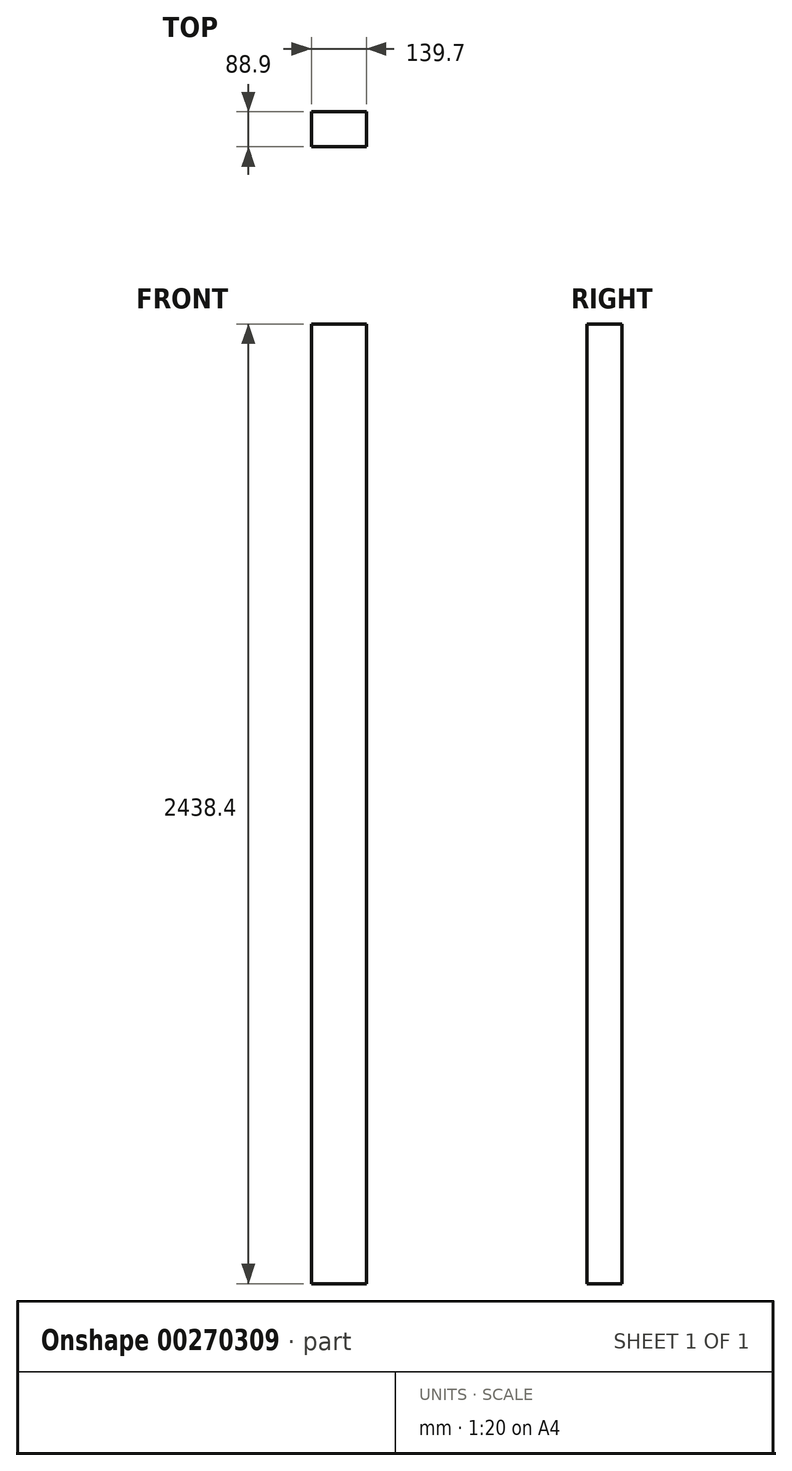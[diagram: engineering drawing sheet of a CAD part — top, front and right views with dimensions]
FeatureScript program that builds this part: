
annotation { "Feature Type Name" : "Feature", "Feature Type Description" : "" }
export const myFeature = defineFeature(function(context is Context, id is Id, definition is map)
    precondition{}
    {
        {
            var Q0;
            Q0=qCreatedBy(makeId("Top.planeOp"),FACE);
            var sketch = newSketch(context, id + "F0", { "sketchPlane" : qUnion([Q0])});
            skLineSegment(sketch, "E0.bottom", {"start": v(69.85, -44.45) * mm, "end": v(-69.85, -44.45) * mm});
            skLineSegment(sketch, "E0.top", {"start": v(69.85, 44.45) * mm, "end": v(-69.85, 44.45) * mm});
            skLineSegment(sketch, "E0.left", {"start": v(69.85, -44.45) * mm, "end": v(69.85, 44.45) * mm});
            skLineSegment(sketch, "E0.right", {"start": v(-69.85, -44.45) * mm, "end": v(-69.85, 44.45) * mm});
            skPoint(sketch, "E0.middle", {"position": v(0, 0) * mm});
            skSolve(sketch);
        }
        {
            var Q0;
            Q0=makeQuery(id+"F0.imprint","IMPRINT",FACE,{"disambiguationData":[TD([[makeQuery(id+"F0.imprint","IMPRINT",EDGE,{"derivedFrom":sQuery(id+"F0.wireOp",EDGE,"E0.bottom")}),-1.0]])]});
            extrude(context, id + "F1", {"entities" : qUnion([Q0]), "endBound" : BoundingType.SYMMETRIC, "depth" : 2438.4 * mm});
        }
    });
